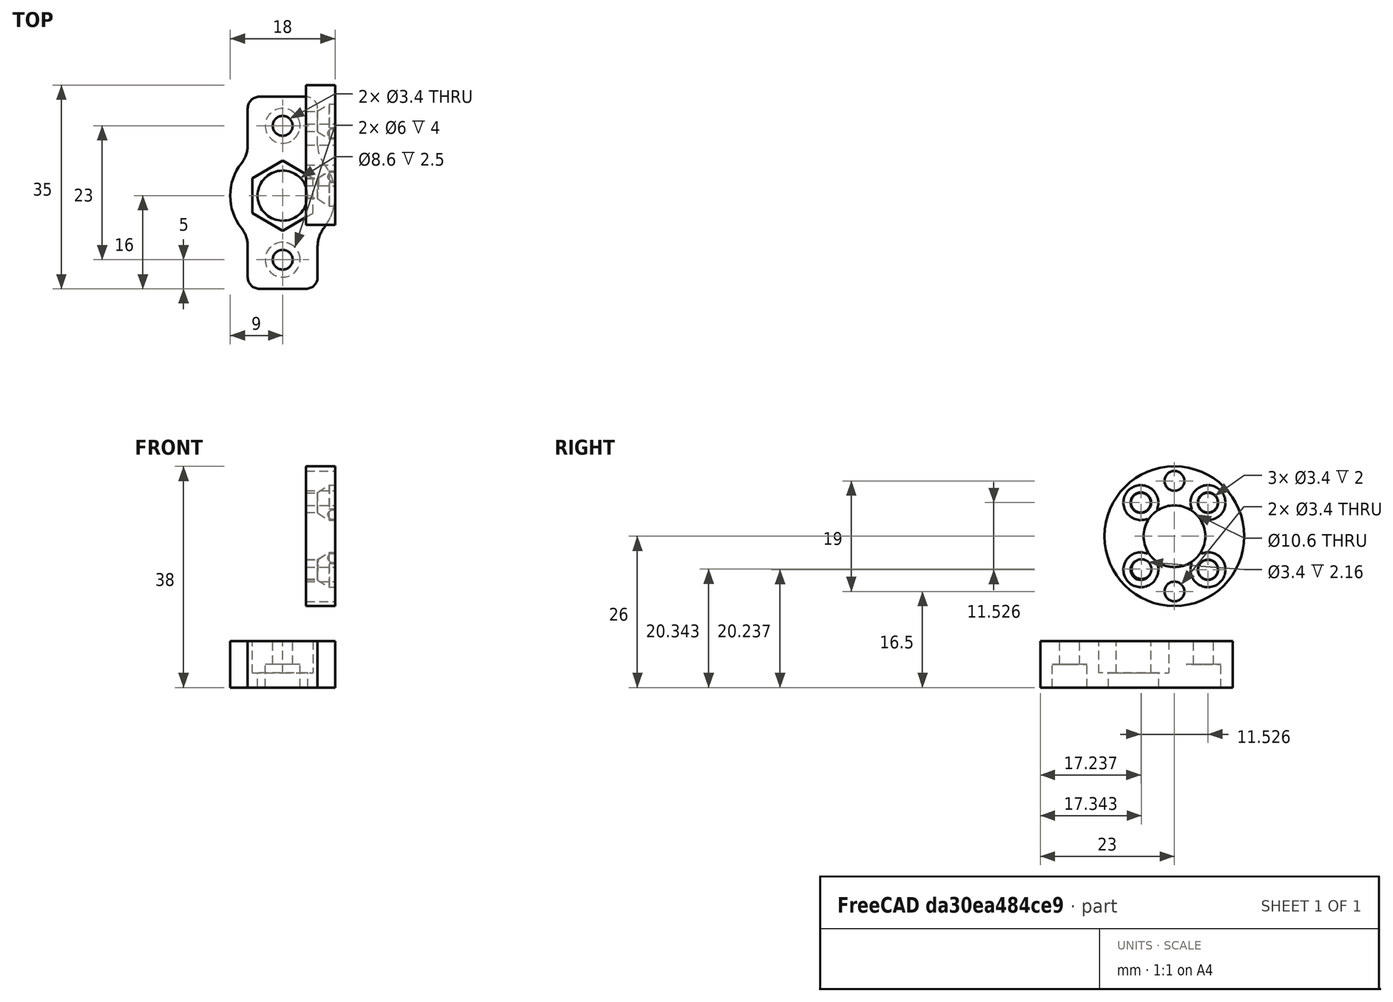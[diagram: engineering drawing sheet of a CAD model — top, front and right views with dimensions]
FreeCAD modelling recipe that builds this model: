
FCSTD DOCUMENT  (FreeCAD 0.18.3R)
Label: screw-drive-adapter
License: All rights reserved
LicenseURL: http://en.wikipedia.org/wiki/All_rights_reserved
objects: Part::Cylinder×16, Part::MultiFuse×9, Part::Cut×8, Part::Feature×8, Part::Chamfer×2, Part::Box×2, Part::Fillet×2, Mesh::Feature×1, Part::Cone×1
note: 48 computed .brp shape members not serialized (recipe doc carries the construction recipe); baked Part::Feature solids carry a one-line shape summary decoded from their .brp

FEATURE [Mesh::Feature] mmu2_selector_finda  label="mmu2-selector-finda"
  Placement = pos=(-59,4,61) rot=(0,0,1;0rad)
FEATURE [Part::Cylinder] Cylinder
  Angle = 360
  AttacherType = Attacher::AttachEngine3D
  Height = 50
  Placement = pos=(23,3,-43) rot=(0,1,0;1.5708rad)
  Radius = 5.3
FEATURE [Part::Cylinder] Cylinder001
  Angle = 360
  AttacherType = Attacher::AttachEngine3D
  Height = 5
  Placement = pos=(63,3,-43) rot=(0,1,0;1.5708rad)
  Radius = 12
FEATURE [Part::Cylinder] Cylinder002
  Angle = 360
  AttacherType = Attacher::AttachEngine3D
  Height = 50
  Placement = pos=(23,3,-52.5) rot=(0,1,0;1.5708rad)
  Radius = 1.7
FEATURE [Part::Cylinder] Cylinder003
  Angle = 360
  AttacherType = Attacher::AttachEngine3D
  Height = 10
  Placement = pos=(60,11.15,-43) rot=(0,1,0;1.5708rad)
  Radius = 1.7
FEATURE [Part::Cylinder] Cylinder005
  Angle = 360
  AttacherType = Attacher::AttachEngine3D
  Height = 50
  Placement = pos=(23,3,-33.5) rot=(0,1,0;1.5708rad)
  Radius = 1.7
FEATURE [Part::MultiFuse] Fusion  label="body-screws"
  Shapes = -> [Cylinder005,Cylinder002]
FEATURE [Part::Cut] Cut  label="blank"
  Base = -> Cylinder001
  Tool = -> Cylinder
FEATURE [Part::Cut] Cut001
  Base = -> Cut
  Tool = -> Fusion
FEATURE [Part::Cylinder] Cylinder006
  Angle = 360
  AttacherType = Attacher::AttachEngine3D
  Height = 10
  Placement = pos=(60,-5,-43) rot=(0,1,0;1.5708rad)
  Radius = 1.7
FEATURE [Part::Cylinder] Cylinder007
  Angle = 360
  AttacherType = Attacher::AttachEngine3D
  Height = 10
  Placement = pos=(60,3,-51.15) rot=(0,1,0;1.5708rad)
  Radius = 1.7
FEATURE [Part::Cylinder] Cylinder008
  Angle = 360
  AttacherType = Attacher::AttachEngine3D
  Height = 10
  Placement = pos=(60,3,-34.85) rot=(0,1,0;1.5708rad)
  Radius = 1.7
FEATURE [Part::MultiFuse] Fusion001  label="4-holes"
  Placement = pos=(0,-29.5269,-14.7157) rot=(1,0,0;0.785398rad)
  Shapes = -> [Cylinder003,Cylinder006,Cylinder007,Cylinder008]
FEATURE [Part::Cut] Cut002
  Base = -> Cut001
  Tool = -> Fusion001
FEATURE [Part::Cone] Cone
  Angle = 360
  AttacherType = Attacher::AttachEngine3D
  Height = 2
  Placement = pos=(64,3,-43) rot=(0,1,0;1.5708rad)
  Radius1 = 1.75
  Radius2 = 3
FEATURE [Part::Cylinder] Cylinder009
  Angle = 360
  AttacherType = Attacher::AttachEngine3D
  Height = 10
  Placement = pos=(66,3,-43) rot=(0,1,0;1.5708rad)
  Radius = 3
FEATURE [Part::MultiFuse] Fusion002  label="countersink"
  Placement = pos=(0,0,8.15) rot=(0,0,1;0rad)
  Shapes = -> [Cone,Cylinder009]
FEATURE [Part::Feature] Fusion002001
  Placement = pos=(0,-48.15,-46) rot=(1,0,0;1.5708rad)
  shape: bbox 12 x 6 x 6 mm, 4 faces (baked)
FEATURE [Part::Feature] Fusion002002
  Placement = pos=(0,6,-94.15) rot=(1,0,0;3.14159rad)
  shape: bbox 12 x 6 x 6 mm, 4 faces (baked)
FEATURE [Part::Feature] Fusion002003
  Placement = pos=(0,54.15,-40) rot=(-1,0,0;1.5708rad)
  shape: bbox 12 x 6 x 6 mm, 4 faces (baked)
FEATURE [Part::MultiFuse] Fusion002004  label="countersinks"
  Placement = pos=(1,-29.5269,-14.7157) rot=(1,0,0;0.785398rad)
  Shapes = -> [Fusion002,Fusion002001,Fusion002003,Fusion002002]
FEATURE [Part::Cut] Cut003
  Base = -> Cut002
  Tool = -> Fusion002004
FEATURE [Part::Chamfer] Chamfer
  Base = -> Cut003
  Edges = 1 edges r=0.5: [Edge31]
FEATURE [Part::Chamfer] Chamfer001  label="adapter"
  Base = -> Chamfer
  Edges = 7 edges r=0.5: [Edge15,Edge21,Edge22,Edge23,Edge24,Edge29,Edge30]
  Placement = pos=(-59,4,61) rot=(0,0,1;0rad)
FEATURE [Part::Cylinder] Cylinder010
  Angle = 360
  AttacherType = Attacher::AttachEngine3D
  Height = 8
  Placement = pos=(0,0,-9) rot=(0,0,1;0rad)
  Radius = 8
FEATURE [Part::Box] Box  label="Cube"
  AttacherType = Attacher::AttachEngine3D
  Height = 8
  Length = 12
  Placement = pos=(-6,-16,-8) rot=(0,0,1;0rad)
  Width = 33
FEATURE [Part::Box] Box001  label="Cube001"
  AttacherType = Attacher::AttachEngine3D
  Height = 10
  Length = 10
  Placement = pos=(5.2,-7,-10) rot=(0,0,1;0rad)
  Width = 12
FEATURE [Part::Feature] Box001001
  Placement = pos=(8.66218,1.00333,-10) rot=(0,0,1;1.0472rad)
  shape: bbox 15.39 x 14.66 x 10 mm, 6 faces (baked)
FEATURE [Part::Feature] Box001002
  Placement = pos=(3.46218,8.00333,-10) rot=(0,0,1;2.0944rad)
  shape: bbox 15.39 x 14.66 x 10 mm, 6 faces (baked)
FEATURE [Part::Feature] Box001003
  Placement = pos=(-5.2,7,-10) rot=(0,0,1;3.14159rad)
  shape: bbox 10 x 12 x 10 mm, 6 faces (baked)
FEATURE [Part::Feature] Box001004
  Placement = pos=(-8.66218,-1.00333,-10) rot=(0,0,1;4.18879rad)
  shape: bbox 15.39 x 14.66 x 10 mm, 6 faces (baked)
FEATURE [Part::Feature] Box001005
  Placement = pos=(-3.46218,-8.00333,-10) rot=(0,0,-1;1.0472rad)
  shape: bbox 15.39 x 14.66 x 10 mm, 6 faces (baked)
FEATURE [Part::MultiFuse] Fusion002005
  Shapes = -> [Box001,Box001003,Box001002,Box001004,Box001005,Box001001]
FEATURE [Part::Cut] Cut004  label="M6-nut"
  Base = -> Cylinder010
  Placement = pos=(0,0,3.5) rot=(0,0,1;0rad)
  Tool = -> Fusion002005
FEATURE [Part::Cylinder] Cylinder011
  Angle = 360
  AttacherType = Attacher::AttachEngine3D
  Height = 20
  Placement = pos=(0,0,-13) rot=(0,0,1;0rad)
  Radius = 4.3
FEATURE [Part::Cylinder] Cylinder013
  Angle = 360
  AttacherType = Attacher::AttachEngine3D
  Height = 8
  Placement = pos=(0,0,-8) rot=(0,0,1;0rad)
  Radius = 9
FEATURE [Part::MultiFuse] Fusion002006
  Shapes = -> [Cylinder013,Box]
FEATURE [Part::MultiFuse] Fusion002007
  Shapes = -> [Cut004,Cylinder011]
FEATURE [Part::Cut] Cut005
  Base = -> Fusion002006
  Tool = -> Fusion002007
FEATURE [Part::Cylinder] Cylinder014
  Angle = 360
  AttacherType = Attacher::AttachEngine3D
  Height = 10
  Placement = pos=(0,12,-9) rot=(0,0,1;0rad)
  Radius = 1.7
FEATURE [Part::Cylinder] Cylinder015
  Angle = 360
  AttacherType = Attacher::AttachEngine3D
  Height = 10
  Placement = pos=(0,-11,-9) rot=(0,0,1;0rad)
  Radius = 1.7
FEATURE [Part::MultiFuse] Fusion002008
  Shapes = -> [Cylinder014,Cylinder015]
FEATURE [Part::Cut] Cut006
  Base = -> Cut005
  Tool = -> Fusion002008
FEATURE [Part::Cylinder] Cylinder017
  Angle = 360
  AttacherType = Attacher::AttachEngine3D
  Height = 10
  Placement = pos=(0,12,-14) rot=(0,0,1;0rad)
  Radius = 3
FEATURE [Part::Cylinder] Cylinder018
  Angle = 360
  AttacherType = Attacher::AttachEngine3D
  Height = 10
  Placement = pos=(0,-11,-14) rot=(0,0,1;0rad)
  Radius = 3
FEATURE [Part::MultiFuse] Fusion002009
  Shapes = -> [Cylinder017,Cylinder018]
FEATURE [Part::Cut] Cut007
  Base = -> Cut006
  Tool = -> Fusion002009
FEATURE [Part::Fillet] Fillet
  Base = -> Cut007
  Edges = 4 edges r=2: [Edge11,Edge14,Edge31,Edge44]
FEATURE [Part::Fillet] Fillet001  label="pneumatic-holder"
  Base = -> Fillet
  Edges = 4 edges r=5: [Edge3,Edge24,Edge38,Edge50]
